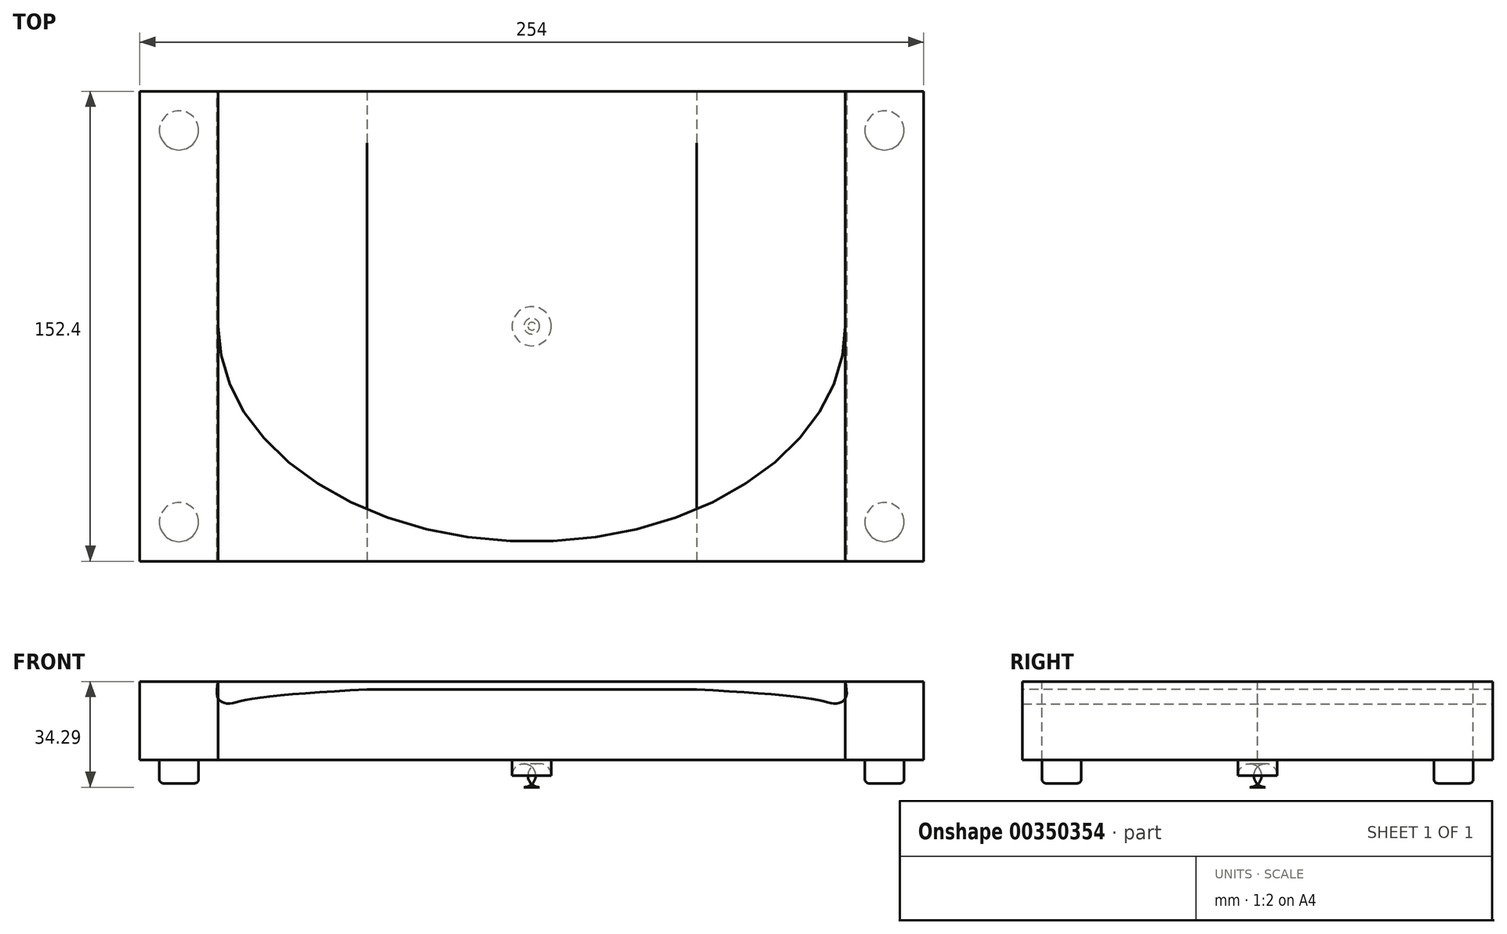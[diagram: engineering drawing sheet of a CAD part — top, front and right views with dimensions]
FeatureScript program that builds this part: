
annotation { "Feature Type Name" : "Feature", "Feature Type Description" : "" }
export const myFeature = defineFeature(function(context is Context, id is Id, definition is map)
    precondition{}
    {
        {
            var Q0;
            Q0=qCreatedBy(makeId("Top.planeOp"),FACE);
            var sketch = newSketch(context, id + "F0", { "sketchPlane" : qUnion([Q0])});
            skLineSegment(sketch, "E0.bottom", {"start": v(0, 0) * mm, "end": v(254, 0) * mm});
            skLineSegment(sketch, "E0.top", {"start": v(0, 152.4) * mm, "end": v(254, 152.4) * mm});
            skLineSegment(sketch, "E0.left", {"start": v(0, 0) * mm, "end": v(0, 152.4) * mm});
            skLineSegment(sketch, "E0.right", {"start": v(254, 0) * mm, "end": v(254, 152.4) * mm});
            skSolve(sketch);
        }
        {
            var Q0;
            Q0 = qSketchRegion(id + "F0", true);
            extrude(context, id + "F1", {"entities" : qUnion([Q0]), "depth" : 25.4 * mm});
        }
        {
            var Q0;
            Q0=makeQuery(id+"F1.opExtrude","SWEPT_FACE",FACE,{"disambiguationData":[OSD([sQuery(id+"F0.wireOp",EDGE,"E0.bottom")])]});
            var sketch = newSketch(context, id + "F2", { "sketchPlane" : qUnion([Q0])});
            skLineSegment(sketch, "E1", {"start": v(127, 25.4) * mm, "end": v(127, 0) * mm});
            skLineSegment(sketch, "E2", {"start": v(127, 25.4) * mm, "end": v(228.6, 25.4) * mm});
            skLineSegment(sketch, "E3", {"start": v(127, 25.4) * mm, "end": v(25.4, 25.4) * mm});
            skFitSpline(sketch, "E4", {"points": [v(25.4, 25.4) * mm, v(25.4, 19.9) * mm, v(28.43, 18.18) * mm, v(33.83, 19.32) * mm, v(127, 25.4) * mm], "startDerivative": vector(-7.76, -43.3) * mm, "endDerivative": vector(205.13, 9.01) * mm});
            skFitSpline(sketch, "E5.MirrorCS", {"points": [v(228.6, 25.4) * mm, v(228.6, 19.9) * mm, v(225.57, 18.18) * mm, v(220.17, 19.32) * mm, v(127, 25.4) * mm], "startDerivative": vector(7.76, -43.3) * mm, "endDerivative": vector(-205.13, 9.01) * mm});
            skSolve(sketch);
        }
        {
            var Q0;
            Q0=makeQuery(id+"F2.imprint","IMPRINT",FACE,{"disambiguationData":[TD([[makeQuery(id+"F2.imprint","IMPRINT",EDGE,{"derivedFrom":sQuery(id+"F2.wireOp",EDGE,"E2")}),-1.0]])]});
            var Q1;
            Q1=makeQuery(id+"F2.imprint","IMPRINT",FACE,{"disambiguationData":[TD([[makeQuery(id+"F2.imprint","IMPRINT",EDGE,{"derivedFrom":sQuery(id+"F2.wireOp",EDGE,"E3")}),-1.0]])]});
            extrude(context, id + "F3", {"entities" : qUnion([Q0, Q1]), "operationType" : NewBodyOperationType.REMOVE, "oppositeDirection" : true, "depth" : 254 * mm});
        }
        {
            var Q0;
            Q0=makeQuery(id+"F1.opExtrude","CAP_FACE",FACE,{"disambiguationData":[OSD([sQuery(id+"F0.wireOp",EDGE,"E0.bottom"),sQuery(id+"F0.wireOp",EDGE,"E0.top"),sQuery(id+"F0.wireOp",EDGE,"E0.left"),sQuery(id+"F0.wireOp",EDGE,"E0.right")])],"isStart":false});
            var sketch = newSketch(context, id + "F4", { "sketchPlane" : qUnion([Q0])});
            skEllipse(sketch, "E6", {"center": v(127, 76.2) * mm, "majorRadius": 101.6 * mm, "minorRadius": 69.85 * mm, "majorAxis": v(1, 0)});
            skLineSegment(sketch, "E7", {"start": v(228.6, 152.4) * mm, "end": v(228.6, 0) * mm});
            skLineSegment(sketch, "E8", {"start": v(25.4, 0) * mm, "end": v(25.4, 152.4) * mm});
            skLineSegment(sketch, "E9", {"start": v(25.4, 152.4) * mm, "end": v(228.6, 152.4) * mm});
            skLineSegment(sketch, "E10", {"start": v(228.6, 0) * mm, "end": v(25.4, 0) * mm});
            skSolve(sketch);
        }
        {
            var Q0;
            Q0 = qSketchRegion(id + "F4", true);
            extrude(context, id + "F5", {"entities" : qUnion([Q0]), "operationType" : NewBodyOperationType.REMOVE, "oppositeDirection" : true, "depth" : 2.54 * mm});
        }
        {
            var Q0;
            {var subQ0=sQuery(id+"F4.wireOp",EDGE,"E9");var subQ1=sQuery(id+"F4.wireOp",EDGE,"E6");var subQ2=makeQuery(id+"F4.imprint","INTERSECT",VERTEX,{"disambiguationData":[OD(1.0)],"derivedFrom":[subQ1,subQ0]});Q0=makeQuery(id+"F4.imprint","IMPRINT",FACE,{"disambiguationData":[TD([[makeQuery(id+"F4.imprint","IMPRINT",EDGE,{"disambiguationData":[TD([[subQ2,-1.0]])],"derivedFrom":subQ1}),-1.0]])]});}
            var Q1;
            {var subQ0=sQuery(id+"F4.wireOp",EDGE,"E9");var subQ1=sQuery(id+"F4.wireOp",EDGE,"E6");var subQ2=makeQuery(id+"F4.imprint","INTERSECT",VERTEX,{"disambiguationData":[OD(0.0)],"derivedFrom":[subQ1,subQ0]});Q1=makeQuery(id+"F4.imprint","IMPRINT",FACE,{"disambiguationData":[TD([[makeQuery(id+"F4.imprint","IMPRINT",EDGE,{"disambiguationData":[TD([[subQ2,1.0]])],"derivedFrom":subQ1}),-1.0]])]});}
            var Q2;
            {var subQ5=sQuery(id+"F4.wireOp",EDGE,"E10");Q2=makeQuery(id+"F4.imprint","IMPRINT",FACE,{"disambiguationData":[TD([[makeQuery(id+"F4.imprint","IMPRINT",EDGE,{"derivedFrom":subQ5}),-1.0]])]});}
            extrude(context, id + "F6", {"entities" : qUnion([Q0, Q1, Q2]), "oppositeDirection" : true, "depth" : 25.4 * mm});
        }
        {
            var Q0;
            Q0=makeQuery(id+"F5.boolean.opBoolean","COPY",FACE,{"derivedFrom":makeQuery(id+"F5.opExtrude","CAP_FACE",FACE,{"disambiguationData":[OSD([sQuery(id+"F4.wireOp",EDGE,"E6"),sQuery(id+"F4.wireOp",EDGE,"E7"),sQuery(id+"F4.wireOp",EDGE,"E8"),sQuery(id+"F4.wireOp",EDGE,"E9"),sQuery(id+"F4.wireOp",EDGE,"E10")])],"isStart":false})});
            var sketch = newSketch(context, id + "F7", { "sketchPlane" : qUnion([Q0])});
            skCircle(sketch, "E11", {"center": v(127, 76.2) * mm, "radius": 6.35 * mm});
            skSolve(sketch);
        }
        {
            var Q0;
            Q0 = qSketchRegion(id + "F7", true);
            extrude(context, id + "F8", {"entities" : qUnion([Q0]), "operationType" : NewBodyOperationType.ADD, "oppositeDirection" : true, "depth" : 31.75 * mm});
        }
        {
            var Q0;
            Q0=makeQuery(id+"F8.opExtrude","CAP_FACE",FACE,{"disambiguationData":[OSD([sQuery(id+"F7.wireOp",EDGE,"E11")])],"isStart":false});
            fillet(context, id + "F9", {"entities" : qUnion([Q0]), "radius" : 3.8 * mm, "tangentPropagation" : true, "allowEdgeOverflow" : false});
        }
        {
            var Q0;
            Q0=makeQuery(id+"F1.opExtrude","CAP_FACE",FACE,{"disambiguationData":[OSD([sQuery(id+"F0.wireOp",EDGE,"E0.bottom"),sQuery(id+"F0.wireOp",EDGE,"E0.top"),sQuery(id+"F0.wireOp",EDGE,"E0.left"),sQuery(id+"F0.wireOp",EDGE,"E0.right")])],"isStart":true});
            var sketch = newSketch(context, id + "F10", { "sketchPlane" : qUnion([Q0])});
            skCircle(sketch, "E12", {"center": v(12.7, -12.7) * mm, "radius": 6.35 * mm});
            skCircle(sketch, "E13", {"center": v(12.7, -139.7) * mm, "radius": 6.35 * mm});
            skCircle(sketch, "E14.MirrorC", {"center": v(241.3, -12.7) * mm, "radius": 6.35 * mm});
            skCircle(sketch, "E15.MirrorC", {"center": v(241.3, -139.7) * mm, "radius": 6.35 * mm});
            skSolve(sketch);
        }
        {
            var Q0;
            Q0 = qSketchRegion(id + "F10", true);
            extrude(context, id + "F11", {"entities" : qUnion([Q0]), "operationType" : NewBodyOperationType.ADD, "depth" : 7.62 * mm});
        }
        {
            var Q0;
            Q0=makeQuery(id+"F11.opExtrude","CAP_FACE",FACE,{"disambiguationData":[OSD([sQuery(id+"F10.wireOp",EDGE,"E15.MirrorC")])],"isStart":false});
            var Q1;
            Q1=makeQuery(id+"F11.opExtrude","CAP_FACE",FACE,{"disambiguationData":[OSD([sQuery(id+"F10.wireOp",EDGE,"E14.MirrorC")])],"isStart":false});
            var Q2;
            Q2=makeQuery(id+"F11.opExtrude","CAP_FACE",FACE,{"disambiguationData":[OSD([sQuery(id+"F10.wireOp",EDGE,"E13")])],"isStart":false});
            var Q3;
            Q3=makeQuery(id+"F11.opExtrude","CAP_FACE",FACE,{"disambiguationData":[OSD([sQuery(id+"F10.wireOp",EDGE,"E12")])],"isStart":false});
            fillet(context, id + "F12", {"entities" : qUnion([Q0, Q1, Q2, Q3]), "radius" : 1.27 * mm, "tangentPropagation" : true, "allowEdgeOverflow" : false});
        }
    });
